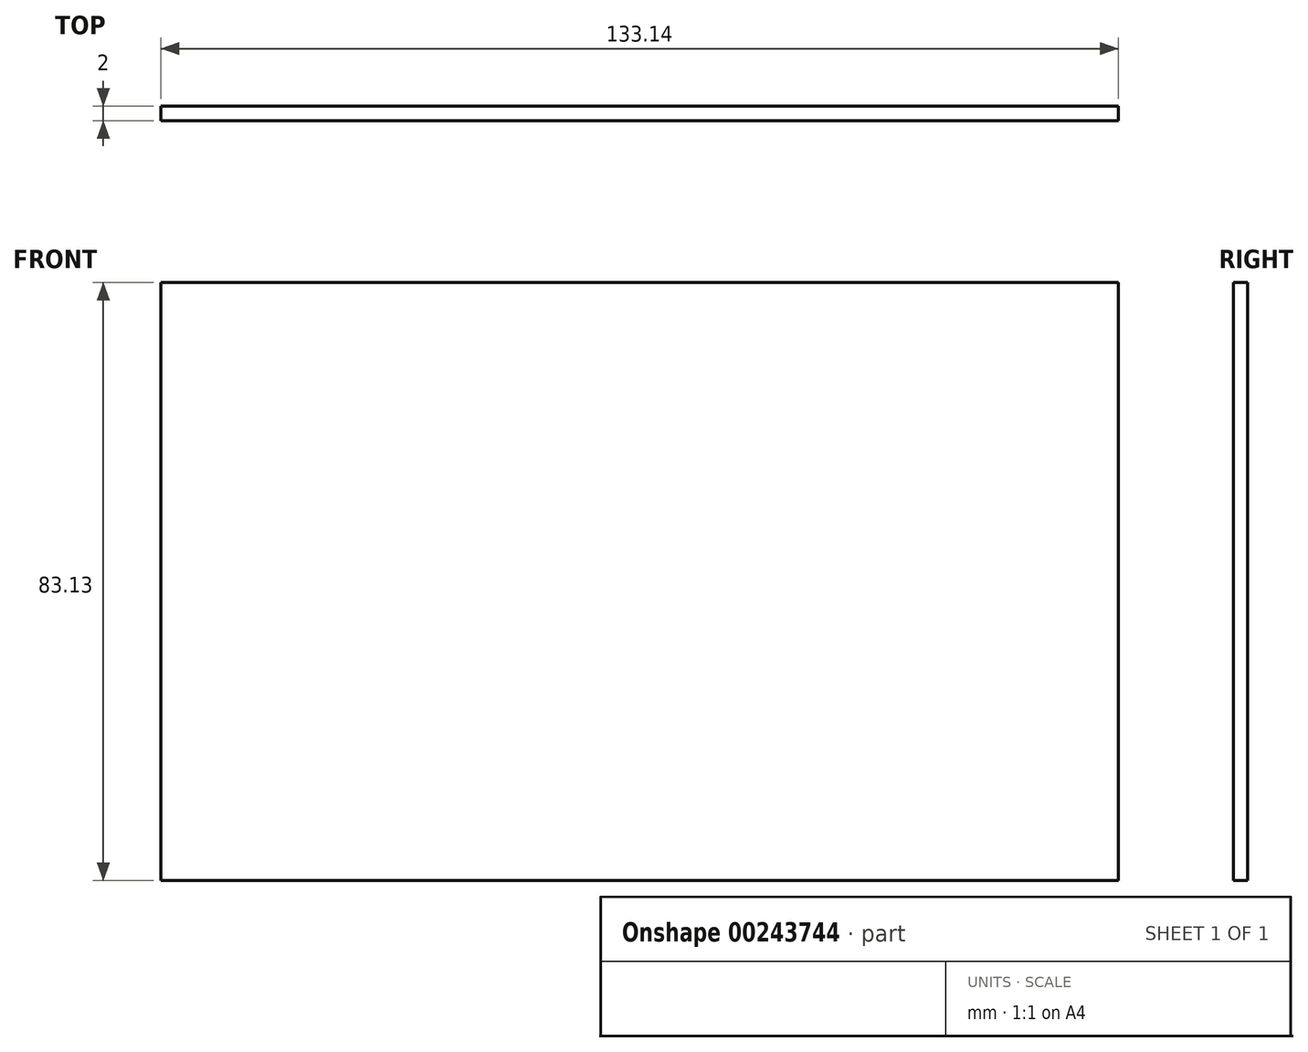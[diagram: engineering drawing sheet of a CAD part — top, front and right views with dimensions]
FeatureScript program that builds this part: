
annotation { "Feature Type Name" : "Feature", "Feature Type Description" : "" }
export const myFeature = defineFeature(function(context is Context, id is Id, definition is map)
    precondition{}
    {
        {
            var Q0;
            Q0=qCreatedBy(makeId("Front.planeOp"),FACE);
            var sketch = newSketch(context, id + "F0", { "sketchPlane" : qUnion([Q0])});
            skLineSegment(sketch, "E0.bottom", {"start": v(-108.06, 55.32) * mm, "end": v(25.08, 55.32) * mm});
            skLineSegment(sketch, "E0.top", {"start": v(-108.06, -27.81) * mm, "end": v(25.08, -27.81) * mm});
            skLineSegment(sketch, "E0.left", {"start": v(-108.06, 55.32) * mm, "end": v(-108.06, -27.81) * mm});
            skLineSegment(sketch, "E0.right", {"start": v(25.08, 55.32) * mm, "end": v(25.08, -27.81) * mm});
            skSolve(sketch);
        }
        {
            var Q0;
            Q0=makeQuery(id+"F0.imprint","IMPRINT",FACE,{"disambiguationData":[TD([[makeQuery(id+"F0.imprint","IMPRINT",EDGE,{"derivedFrom":sQuery(id+"F0.wireOp",EDGE,"E0.bottom")}),-1.0]])]});
            extrude(context, id + "F1", {"entities" : qUnion([Q0]), "depth" : 2 * mm});
        }
    });
